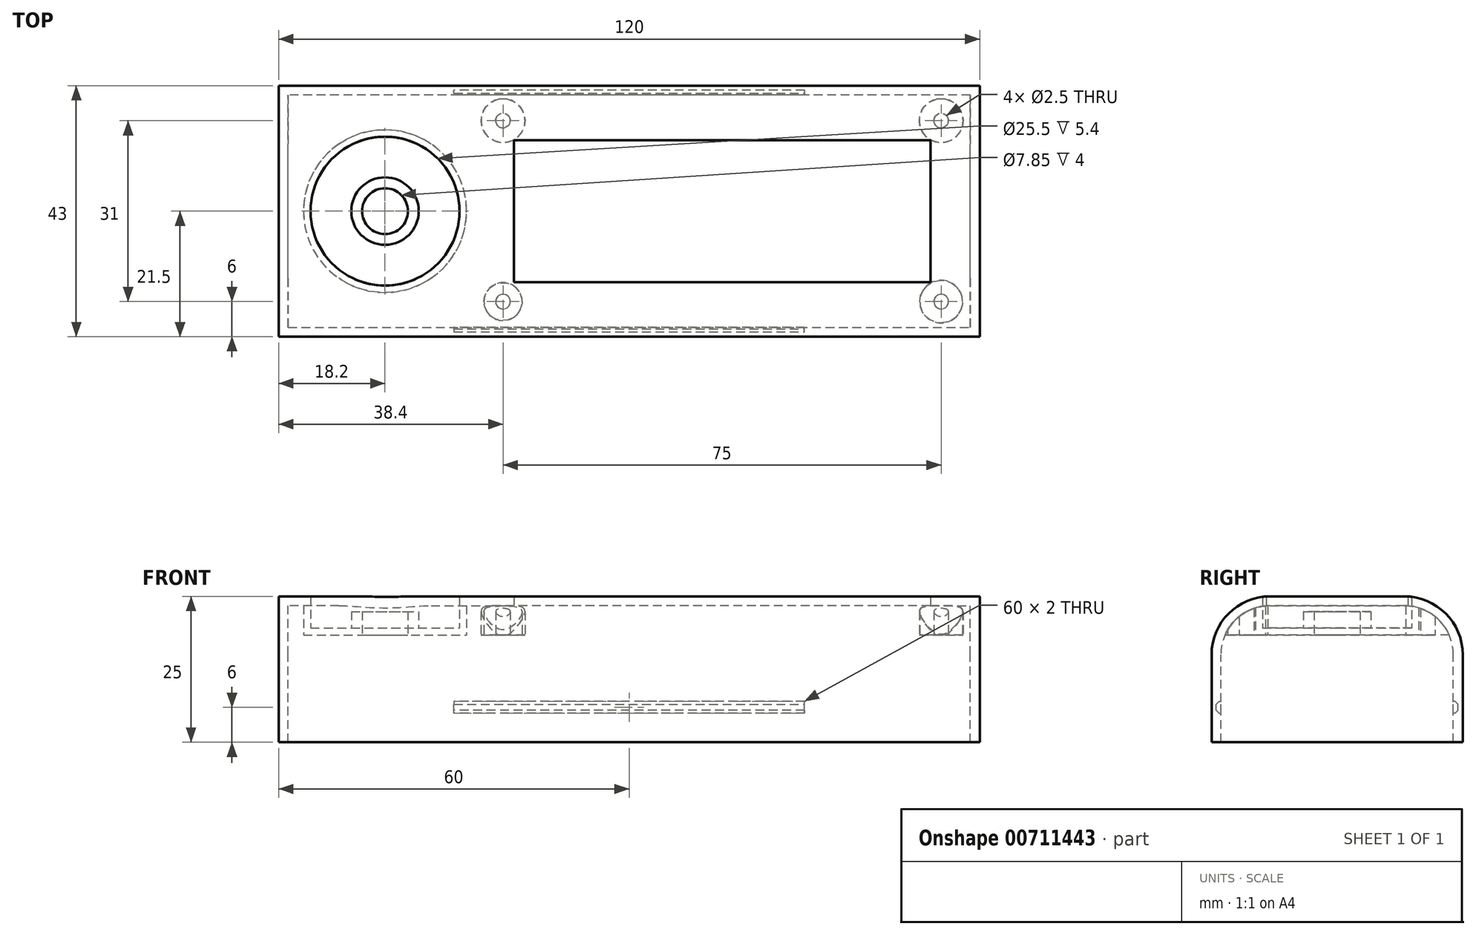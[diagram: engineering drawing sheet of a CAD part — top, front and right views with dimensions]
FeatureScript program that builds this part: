
annotation { "Feature Type Name" : "Feature", "Feature Type Description" : "" }
export const myFeature = defineFeature(function(context is Context, id is Id, definition is map)
    precondition{}
    {
        {
            var Q0;
            Q0=qCreatedBy(makeId("Right.planeOp"),FACE);
            var sketch = newSketch(context, id + "F0", { "sketchPlane" : qUnion([Q0])});
            skLineSegment(sketch, "E0.bottom", {"start": v(-21.5, 0) * mm, "end": v(21.5, 0) * mm});
            skLineSegment(sketch, "E0.top", {"start": v(-11.5, 25) * mm, "end": v(11.5, 25) * mm});
            skLineSegment(sketch, "E0.left", {"start": v(-21.5, 0) * mm, "end": v(-21.5, 15) * mm});
            skLineSegment(sketch, "E0.right", {"start": v(21.5, 0) * mm, "end": v(21.5, 15) * mm});
            skPoint(sketch, "E1.visualSharp", {"position": v(-21.5, 25) * mm});
            skArc(sketch, "E1.filletArc", {"start": v(-11.5, 25) * mm, "mid": v(-18.57, 22.07) * mm, "end": v(-21.5, 15) * mm});
            skPoint(sketch, "E2.visualSharp", {"position": v(21.5, 25) * mm});
            skArc(sketch, "E2.filletArc", {"start": v(21.5, 15) * mm, "mid": v(18.57, 22.07) * mm, "end": v(11.5, 25) * mm});
            skSolve(sketch);
        }
        {
            var Q0;
            Q0=makeQuery(id+"F0.imprint","IMPRINT",FACE,{"disambiguationData":[TD([[makeQuery(id+"F0.imprint","IMPRINT",EDGE,{"derivedFrom":sQuery(id+"F0.wireOp",EDGE,"E0.bottom")}),1.0]])]});
            extrude(context, id + "F1", {"entities" : qUnion([Q0]), "endBound" : BoundingType.SYMMETRIC, "depth" : 120 * mm, "offsetDistance" : 25 * mm});
        }
        {
            var Q0;
            Q0=makeQuery(id+"F1.opExtrude","SWEPT_FACE",FACE,{"disambiguationData":[OSD([sQuery(id+"F0.wireOp",EDGE,"E0.bottom")])]});
            shell(context, id + "F2", {"entities" : qUnion([Q0]), "thickness" : 1.6 * mm});
        }
        {
            var Q0;
            Q0=makeQuery(id+"F2.opShell","OFFSET_FACE",FACE,{"disambiguationData":[OSD([sQuery(id+"F0.wireOp",EDGE,"E0.top")])]});
            cPlane(context, id + "F3", {"entities" : qUnion([Q0]), "cplaneType" : CPlaneType.OFFSET, "offset" : 5 * mm, "width" : 150 * mm, "height" : 150 * mm});
        }
        {
            var Q0;
            Q0=qCreatedBy(id+"F3.planeOp",FACE);
            var sketch = newSketch(context, id + "F4", { "sketchPlane" : qUnion([Q0])});
            skCircle(sketch, "E3", {"center": v(-21.6, 15.5) * mm, "radius": 1.25 * mm});
            skCircle(sketch, "E4", {"center": v(53.4, 15.5) * mm, "radius": 1.25 * mm});
            skCircle(sketch, "E5", {"center": v(-21.6, -15.5) * mm, "radius": 1.25 * mm});
            skCircle(sketch, "E6", {"center": v(53.4, -15.5) * mm, "radius": 1.25 * mm});
            skCircle(sketch, "E7.0", {"center": v(-21.6, 15.5) * mm, "radius": 3.25 * mm});
            skCircle(sketch, "E8.0", {"center": v(53.4, 15.5) * mm, "radius": 3.65 * mm});
            skCircle(sketch, "E9.0", {"center": v(53.4, -15.5) * mm, "radius": 3.75 * mm});
            skCircle(sketch, "E10.0", {"center": v(-21.6, -15.5) * mm, "radius": 3.75 * mm});
            skLineSegment(sketch, "E11.0", {"start": v(58.4, 11.5) * mm, "end": v(58.4, -11.5) * mm, "construction": true});
            skCircle(sketch, "E12", {"center": v(-41.8, 0) * mm, "radius": 12.75 * mm});
            skPoint(sketch, "E13.0", {"position": v(-58.4, 0) * mm});
            skLineSegment(sketch, "E14", {"start": v(-58.4, 0) * mm, "end": v(58.4, 0) * mm, "construction": true});
            skCircle(sketch, "E15.0", {"center": v(-41.8, 0) * mm, "radius": 13.95 * mm});
            skLineSegment(sketch, "E16", {"start": v(-21.6, -15.5) * mm, "end": v(53.4, 15.5) * mm, "construction": true});
            skLineSegment(sketch, "E17.bottom", {"start": v(51.55, -12.15) * mm, "end": v(-19.75, -12.15) * mm});
            skLineSegment(sketch, "E17.top", {"start": v(51.55, 12.15) * mm, "end": v(-19.75, 12.15) * mm});
            skLineSegment(sketch, "E17.left", {"start": v(51.55, -12.15) * mm, "end": v(51.55, 12.15) * mm});
            skLineSegment(sketch, "E17.right", {"start": v(-19.75, -12.15) * mm, "end": v(-19.75, 12.15) * mm});
            skPoint(sketch, "E17.middle", {"position": v(15.9, 0) * mm});
            skSolve(sketch);
        }
        {
            var Q0;
            Q0=makeQuery(id+"F4.imprint","IMPRINT",FACE,{"disambiguationData":[TD([[makeQuery(id+"F4.imprint","IMPRINT",EDGE,{"derivedFrom":sQuery(id+"F4.wireOp",EDGE,"E6")}),-1.0]])]});
            var Q1;
            Q1=makeQuery(id+"F4.imprint","IMPRINT",FACE,{"disambiguationData":[TD([[makeQuery(id+"F4.imprint","IMPRINT",EDGE,{"derivedFrom":sQuery(id+"F4.wireOp",EDGE,"E4")}),-1.0]])]});
            var Q2;
            Q2=makeQuery(id+"F4.imprint","IMPRINT",FACE,{"disambiguationData":[TD([[makeQuery(id+"F4.imprint","IMPRINT",EDGE,{"derivedFrom":sQuery(id+"F4.wireOp",EDGE,"E5")}),-1.0]])]});
            var Q3;
            Q3=makeQuery(id+"F4.imprint","IMPRINT",FACE,{"disambiguationData":[TD([[makeQuery(id+"F4.imprint","IMPRINT",EDGE,{"derivedFrom":sQuery(id+"F4.wireOp",EDGE,"E3")}),-1.0]])]});
            var Q4;
            Q4=makeQuery(id+"F1.opExtrude","SWEPT_BODY",BODY,{"disambiguationData":[OSD([sQuery(id+"F0.wireOp",EDGE,"E0.bottom"),sQuery(id+"F0.wireOp",EDGE,"E0.top"),sQuery(id+"F0.wireOp",EDGE,"E0.left"),sQuery(id+"F0.wireOp",EDGE,"E0.right"),sQuery(id+"F0.wireOp",EDGE,"E1.filletArc"),sQuery(id+"F0.wireOp",EDGE,"E2.filletArc")])]});
            extrude(context, id + "F5", {"entities" : qUnion([Q0, Q1, Q2, Q3]), "operationType" : NewBodyOperationType.ADD, "endBound" : BoundingType.UP_TO_BODY, "oppositeDirection" : true, "depth" : 5 * mm, "endBoundEntityBody" : qUnion([Q4]), "offsetDistance" : 25 * mm});
        }
        {
            var Q0;
            Q0=makeQuery(id+"F4.imprint","IMPRINT",FACE,{"disambiguationData":[TD([[makeQuery(id+"F4.imprint","IMPRINT",EDGE,{"derivedFrom":sQuery(id+"F4.wireOp",EDGE,"E12")}),1.0]])]});
            var Q1;
            Q1=makeQuery(id+"F4.imprint","IMPRINT",FACE,{"disambiguationData":[TD([[makeQuery(id+"F4.imprint","IMPRINT",EDGE,{"derivedFrom":sQuery(id+"F4.wireOp",EDGE,"E17.bottom")}),-1.0]])]});
            extrude(context, id + "F6", {"entities" : qUnion([Q0, Q1]), "operationType" : NewBodyOperationType.REMOVE, "endBound" : BoundingType.THROUGH_ALL, "oppositeDirection" : true, "depth" : 25 * mm, "offsetDistance" : 25 * mm});
        }
        {
            var Q0;
            Q0=makeQuery(id+"F4.imprint","IMPRINT",FACE,{"disambiguationData":[TD([[makeQuery(id+"F4.imprint","IMPRINT",EDGE,{"derivedFrom":sQuery(id+"F4.wireOp",EDGE,"E12")}),1.0]])]});
            var Q1;
            Q1=makeQuery(id+"F4.imprint","IMPRINT",FACE,{"disambiguationData":[TD([[makeQuery(id+"F4.imprint","IMPRINT",EDGE,{"derivedFrom":sQuery(id+"F4.wireOp",EDGE,"E15.0")}),1.0]])]});
            extrude(context, id + "F7", {"entities" : qUnion([Q0, Q1]), "oppositeDirection" : true, "depth" : 1.2 * mm, "offsetDistance" : 25 * mm});
        }
        {
            var Q0;
            Q0=makeQuery(id+"F4.imprint","IMPRINT",FACE,{"disambiguationData":[TD([[makeQuery(id+"F4.imprint","IMPRINT",EDGE,{"derivedFrom":sQuery(id+"F4.wireOp",EDGE,"E12")}),1.0]])]});
            var sketch = newSketch(context, id + "F8", { "sketchPlane" : qUnion([Q0])});
            skPoint(sketch, "E18.0", {"position": v(-41.8, 0) * mm});
            skCircle(sketch, "E19", {"center": v(-41.8, 0) * mm, "radius": 3.92 * mm});
            skCircle(sketch, "E20.0", {"center": v(-41.8, 0) * mm, "radius": 5.77 * mm});
            skSolve(sketch);
        }
        {
            var Q0;
            Q0=makeQuery(id+"F8.imprint","IMPRINT",FACE,{"disambiguationData":[TD([[makeQuery(id+"F8.imprint","IMPRINT",EDGE,{"derivedFrom":sQuery(id+"F8.wireOp",EDGE,"E19")}),1.0]])]});
            extrude(context, id + "F9", {"entities" : qUnion([Q0]), "operationType" : NewBodyOperationType.REMOVE, "endBound" : BoundingType.THROUGH_ALL, "oppositeDirection" : true, "depth" : 25 * mm, "offsetDistance" : 25 * mm});
        }
        {
            var Q0;
            Q0=makeQuery(id+"F8.imprint","IMPRINT",FACE,{"disambiguationData":[TD([[makeQuery(id+"F8.imprint","IMPRINT",EDGE,{"derivedFrom":sQuery(id+"F8.wireOp",EDGE,"E19")}),-1.0]])]});
            var Q1;
            {var subQ0=sQuery(id+"F0.wireOp",EDGE,"E2.filletArc");var subQ1=sQuery(id+"F0.wireOp",EDGE,"E1.filletArc");var subQ2=sQuery(id+"F0.wireOp",EDGE,"E0.right");var subQ3=sQuery(id+"F0.wireOp",EDGE,"E0.left");var subQ4=sQuery(id+"F0.wireOp",EDGE,"E0.top");var subQ5=sQuery(id+"F0.wireOp",EDGE,"E0.bottom");Q1=makeQuery(id+"F6.boolean.opBoolean","SPLIT",FACE,{"disambiguationData":[TD([makeQuery(id+"F2.opShell","OFFSET_FACE",FACE,{"disambiguationData":[OSD([subQ5,subQ4,subQ3,subQ2,subQ1,subQ0]),TDD([makeQuery(id+"F1.opExtrude","CAP_FACE",FACE,{"disambiguationData":[OSD([subQ5,subQ4,subQ3,subQ2,subQ1,subQ0])],"isStart":false})])]})])],"derivedFrom":makeQuery(id+"F2.opShell","OFFSET_FACE",FACE,{"disambiguationData":[OSD([subQ4])]})});}
            var Q2;
            Q2=makeQuery(id+"F7.opExtrude","CAP_FACE",FACE,{"disambiguationData":[OSD([sQuery(id+"F4.wireOp",EDGE,"E12")])],"isStart":false});
            extrude(context, id + "F10", {"entities" : qUnion([Q0]), "operationType" : NewBodyOperationType.ADD, "oppositeDirection" : true, "depth" : 4 * mm, "endBoundEntityFace" : qUnion([Q1]), "offsetDistance" : 25 * mm});
        }
        {
            var Q0;
            Q0=makeQuery(id+"F4.imprint","IMPRINT",FACE,{"disambiguationData":[TD([[makeQuery(id+"F4.imprint","IMPRINT",EDGE,{"derivedFrom":sQuery(id+"F4.wireOp",EDGE,"E12")}),-1.0]])]});
            var Q1;
            {var subQ0=sQuery(id+"F0.wireOp",EDGE,"E2.filletArc");var subQ1=sQuery(id+"F0.wireOp",EDGE,"E1.filletArc");var subQ2=sQuery(id+"F0.wireOp",EDGE,"E0.right");var subQ3=sQuery(id+"F0.wireOp",EDGE,"E0.left");var subQ4=sQuery(id+"F0.wireOp",EDGE,"E0.top");var subQ5=sQuery(id+"F0.wireOp",EDGE,"E0.bottom");Q1=makeQuery(id+"F6.boolean.opBoolean","SPLIT",FACE,{"disambiguationData":[TD([makeQuery(id+"F2.opShell","OFFSET_FACE",FACE,{"disambiguationData":[OSD([subQ5,subQ4,subQ3,subQ2,subQ1,subQ0]),TDD([makeQuery(id+"F1.opExtrude","CAP_FACE",FACE,{"disambiguationData":[OSD([subQ5,subQ4,subQ3,subQ2,subQ1,subQ0])],"isStart":false})])]})])],"derivedFrom":makeQuery(id+"F2.opShell","OFFSET_FACE",FACE,{"disambiguationData":[OSD([subQ4])]})});}
            extrude(context, id + "F11", {"entities" : qUnion([Q0]), "operationType" : NewBodyOperationType.ADD, "endBound" : BoundingType.UP_TO_SURFACE, "oppositeDirection" : true, "depth" : 30.1 * mm, "endBoundEntityFace" : qUnion([Q1]), "offsetDistance" : 25 * mm});
        }
        {
            var Q0;
            Q0=makeQuery(id+"F2.opShell","OFFSET_FACE",FACE,{"disambiguationData":[OSD([sQuery(id+"F0.wireOp",EDGE,"E0.right")])]});
            var sketch = newSketch(context, id + "F12", { "sketchPlane" : qUnion([Q0])});
            skLineSegment(sketch, "E21.bottom", {"start": v(30, 5) * mm, "end": v(-30, 5) * mm});
            skLineSegment(sketch, "E21.top", {"start": v(30, 7) * mm, "end": v(-30, 7) * mm});
            skLineSegment(sketch, "E21.left", {"start": v(30, 5) * mm, "end": v(30, 7) * mm});
            skLineSegment(sketch, "E21.right", {"start": v(-30, 5) * mm, "end": v(-30, 7) * mm});
            skSolve(sketch);
        }
        {
            var Q0;
            Q0=makeQuery(id+"F12.imprint","IMPRINT",FACE,{"disambiguationData":[TD([[makeQuery(id+"F12.imprint","IMPRINT",EDGE,{"derivedFrom":sQuery(id+"F12.wireOp",EDGE,"E21.bottom")}),-1.0]])]});
            extrude(context, id + "F13", {"entities" : qUnion([Q0]), "oppositeDirection" : true, "depth" : 0.8 * mm, "offsetDistance" : 25 * mm});
        }
        {
            var Q0;
            Q0=makeQuery(id+"F13.opExtrude","CAP_EDGE",EDGE,{"disambiguationData":[OSD([sQuery(id+"F12.wireOp",EDGE,"E21.bottom")])],"isStart":false});
            var Q1;
            Q1=makeQuery(id+"F13.opExtrude","CAP_EDGE",EDGE,{"disambiguationData":[OSD([sQuery(id+"F12.wireOp",EDGE,"E21.top")])],"isStart":false});
            chamfer(context, id + "F14", {"entities" : qUnion([Q0, Q1]), "width" : 0.5 * mm, "tangentPropagation" : true});
        }
        {
            var Q0;
            Q0=makeQuery(id+"F13.opExtrude","SWEPT_BODY",BODY,{"disambiguationData":[OSD([sQuery(id+"F12.wireOp",EDGE,"E21.bottom"),sQuery(id+"F12.wireOp",EDGE,"E21.top"),sQuery(id+"F12.wireOp",EDGE,"E21.left"),sQuery(id+"F12.wireOp",EDGE,"E21.right")])]});
            var Q1;
            Q1=qCreatedBy(makeId("Front.planeOp"),FACE);
            mirror(context, id + "F15", {"entities" : qUnion([Q0]), "mirrorPlane" : qUnion([Q1])});
        }
        {
            var Q0;
            Q0=makeQuery(id+"F13.opExtrude","SWEPT_BODY",BODY,{"disambiguationData":[OSD([sQuery(id+"F12.wireOp",EDGE,"E21.bottom"),sQuery(id+"F12.wireOp",EDGE,"E21.top"),sQuery(id+"F12.wireOp",EDGE,"E21.left"),sQuery(id+"F12.wireOp",EDGE,"E21.right")])]});
            var Q1;
            Q1=makeQuery(id+"F15.opPattern","COPY",BODY,{"derivedFrom":makeQuery(id+"F13.opExtrude","SWEPT_BODY",BODY,{"disambiguationData":[OSD([sQuery(id+"F12.wireOp",EDGE,"E21.bottom"),sQuery(id+"F12.wireOp",EDGE,"E21.top"),sQuery(id+"F12.wireOp",EDGE,"E21.left"),sQuery(id+"F12.wireOp",EDGE,"E21.right")])]}),"instanceName":"1"});
            var Q2;
            Q2=makeQuery(id+"F1.opExtrude","SWEPT_BODY",BODY,{"disambiguationData":[OSD([sQuery(id+"F0.wireOp",EDGE,"E0.bottom"),sQuery(id+"F0.wireOp",EDGE,"E0.top"),sQuery(id+"F0.wireOp",EDGE,"E0.left"),sQuery(id+"F0.wireOp",EDGE,"E0.right"),sQuery(id+"F0.wireOp",EDGE,"E1.filletArc"),sQuery(id+"F0.wireOp",EDGE,"E2.filletArc")])]});
            booleanBodies(context, id + "F16", {"operationType" : BooleanOperationType.SUBTRACTION, "tools" : qUnion([Q0, Q1]), "targets" : qUnion([Q2])});
        }
    });
